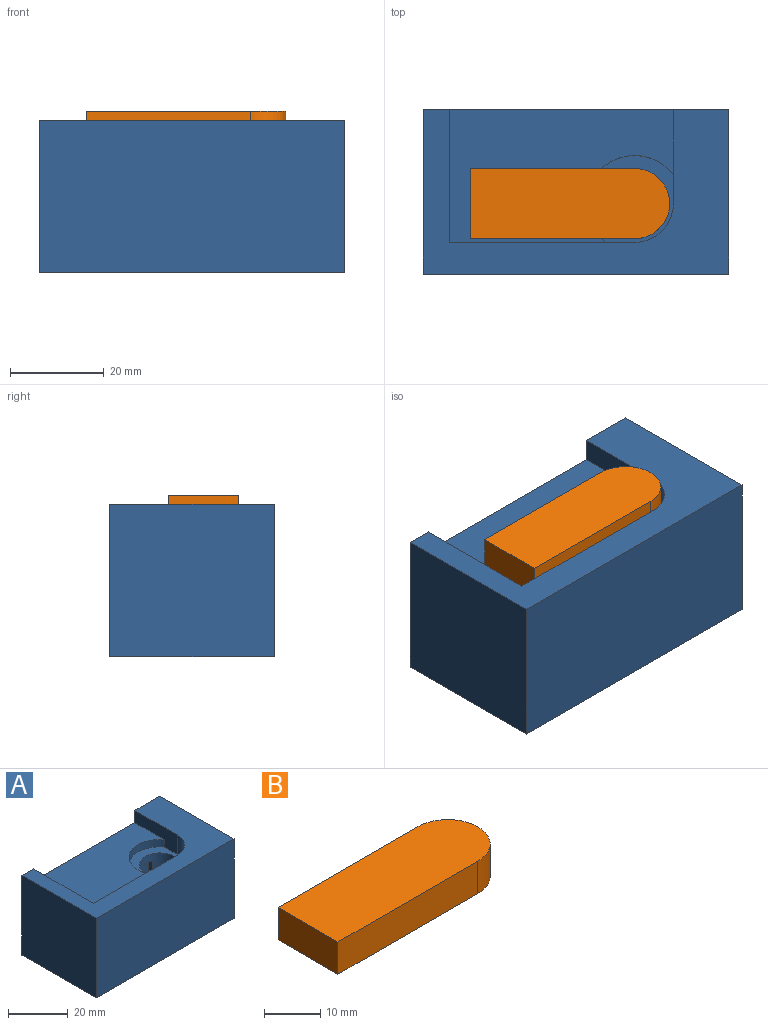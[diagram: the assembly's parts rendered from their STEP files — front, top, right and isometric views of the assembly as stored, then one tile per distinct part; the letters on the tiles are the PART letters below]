
ASSEMBLY  parts=2 mates=1
PART A: 31 faces, bbox 65.1x35.1x32.6 mm
  f0: plane 65x32.5mm, normal (0,1,0), area 1873.8mm2, adj f1,f9,f10,f11,f25,f29,f30
  f1: plane 65x35mm, normal (0,0,1), area 940.8mm2, adj f0,f8,f9,f10,f25,f26,f27,f29
  f2: cylinder r=10.25mm len=18.5mm, axis (0,0,-1), area 105.8mm2, adj f25,f26,f28,f30
  f3: cylinder r=6.75mm len=19.25mm, axis (0,0,-1), area 419mm2, adj f4,f5,f6,f7,f13,f14,f15,f16
  f4: plane 5.5x2.59mm, normal (0,0,-1), area 11.2mm2, adj f3,f12,f13,f17
  f5: plane 5.5x2.59mm, normal (0,0,-1), area 11.2mm2, adj f3,f12,f16,f20
  f6: plane 5.5x2.59mm, normal (0,0,-1), area 11.2mm2, adj f3,f12,f19,f22
  f7: plane 5.5x2.59mm, normal (0,0,-1), area 11.2mm2, adj f3,f12,f14,f23
  f8: plane 65x32.5mm, normal (0,-1,0), area 2112.5mm2, adj f1,f9,f10,f11
  f9: plane 35x32.5mm, normal (1,0,0), area 1137.5mm2, adj f0,f1,f8,f11
  f10: plane 35x32.5mm, normal (-1,0,0), area 1137.5mm2, adj f0,f1,f8,f11
  f11: plane 65x35mm, normal (0,0,-1), area 2034.5mm2, adj f0,f8,f9,f10,f12
  f12: cylinder r=8.75mm len=21.5mm, axis (0,0,-1), area 686.9mm2, adj f4,f5,f6,f7,f11,f13,f14,f15
  f13: plane 16.25x2.14mm, normal (-1,0,0), area 34.8mm2, adj f3,f4,f12,f15
  f14: plane 16.25x2.13mm, normal (0.01,1,0), area 34.7mm2, adj f3,f7,f12,f15
  f15: plane 5.58x5.56mm, normal (0,0,-1), area 13.1mm2, adj f3,f12,f13,f14
  f16: plane 16x2.14mm, normal (0,1,0), area 34.2mm2, adj f3,f5,f12,f18
  f17: plane 16x2.13mm, normal (1,-0.01,0), area 34.1mm2, adj f3,f4,f12,f18
  f18: plane 5.58x5.56mm, normal (0,0,-1), area 13.1mm2, adj f3,f12,f16,f17
  f19: plane 16x2.14mm, normal (1,0,0), area 34.2mm2, adj f3,f6,f12,f21
  f20: plane 16x2.13mm, normal (-0.01,-1,0), area 34.1mm2, adj f3,f5,f12,f21
  f21: plane 5.58x5.56mm, normal (0,0,-1), area 13.1mm2, adj f3,f12,f19,f20
  f22: plane 12.6x2.23mm, normal (-1,0.01,0), area 24.5mm2, adj f3,f6,f12,f24
  f23: plane 12.6x2.24mm, normal (0,-1,0), area 24.6mm2, adj f3,f7,f12,f24
  f24: cone r=8.75mm half-angle=45deg, axis (0,0,-1), area 18.4mm2, adj f3,f12,f22,f23
  f25: plane 20x8mm, normal (-1,0,0), area 118.2mm2, adj f0,f1,f2,f27,f28,f30
  f26: plane 39.5x8mm, normal (0,1,0), area 215.7mm2, adj f1,f2,f27,f28,f29,f30
  f27: cylinder r=8.25mm len=8.25mm, axis (0,0,-1), area 103.7mm2, adj f1,f25,f26,f28
  f28: plane 18.5x18.5mm, normal (0,0,1), area 141.3mm2, adj f2,f3,f25,f26,f27
  f29: plane 28.25x5mm, normal (1,0,0), area 141.3mm2, adj f0,f1,f26,f30
  f30: plane 47.75x28.25mm, normal (0,0,1), area 1049.8mm2, adj f0,f2,f25,f26,f29
PART B: 15 faces, bbox 42.5x15x7 mm
  f0: cone r=6.35mm half-angle=45deg, axis (0,0,-1), area 19.3mm2, adj f7,f9,f11,f14
  f1: cylinder r=7.5mm len=15mm, axis (0,0,1), area 164.9mm2, adj f2,f3,f5,f6
  f2: plane 42.5x15mm, normal (0,0,1), area 613.4mm2, adj f1,f3,f4,f5
  f3: plane 35x7mm, normal (0,-1,0), area 245mm2, adj f1,f2,f4,f6
  f4: plane 15x7mm, normal (-1,0,0), area 105mm2, adj f2,f3,f5,f6
  f5: plane 35x7mm, normal (0,1,0), area 245mm2, adj f1,f2,f4,f6
  f6: plane 42.5x15mm, normal (0,0,-1), area 537.9mm2, adj f1,f3,f4,f5,f7,f8,f10,f12
  f7: cylinder r=6.35mm len=6.2mm, axis (0,0,1), area 22.7mm2, adj f0,f6,f10,f12
  f8: cylinder r=6.35mm len=6.2mm, axis (0,0,1), area 22.7mm2, adj f6,f10,f12,f13
  f9: plane 11.08x2.5mm, normal (-0.93,0,-0.37), area 23.6mm2, adj f0,f10,f13,f14
  f10: plane 11.08x3.5mm, normal (-1,0,0), area 38.8mm2, adj f6,f7,f8,f9
  f11: plane 11.08x2.5mm, normal (0.93,0,-0.37), area 23.6mm2, adj f0,f12,f13,f14
  f12: plane 11.08x3.5mm, normal (1,0,0), area 38.8mm2, adj f6,f7,f8,f11
  f13: cone r=6.35mm half-angle=45deg, axis (0,0,-1), area 19.3mm2, adj f8,f9,f11,f14
  f14: plane 7.7x4.2mm, normal (0,0,-1), area 30.7mm2, adj f0,f9,f11,f13
PLACE A t=(-18.17,-10.82,-4.45)mm
PLACE B t=(-18.17,-10.82,-6.45)mm
MATE fastened B.f8 <-> A.f2  axis (0,0,-1) through (-18.17,-10.82,23.05)mm
